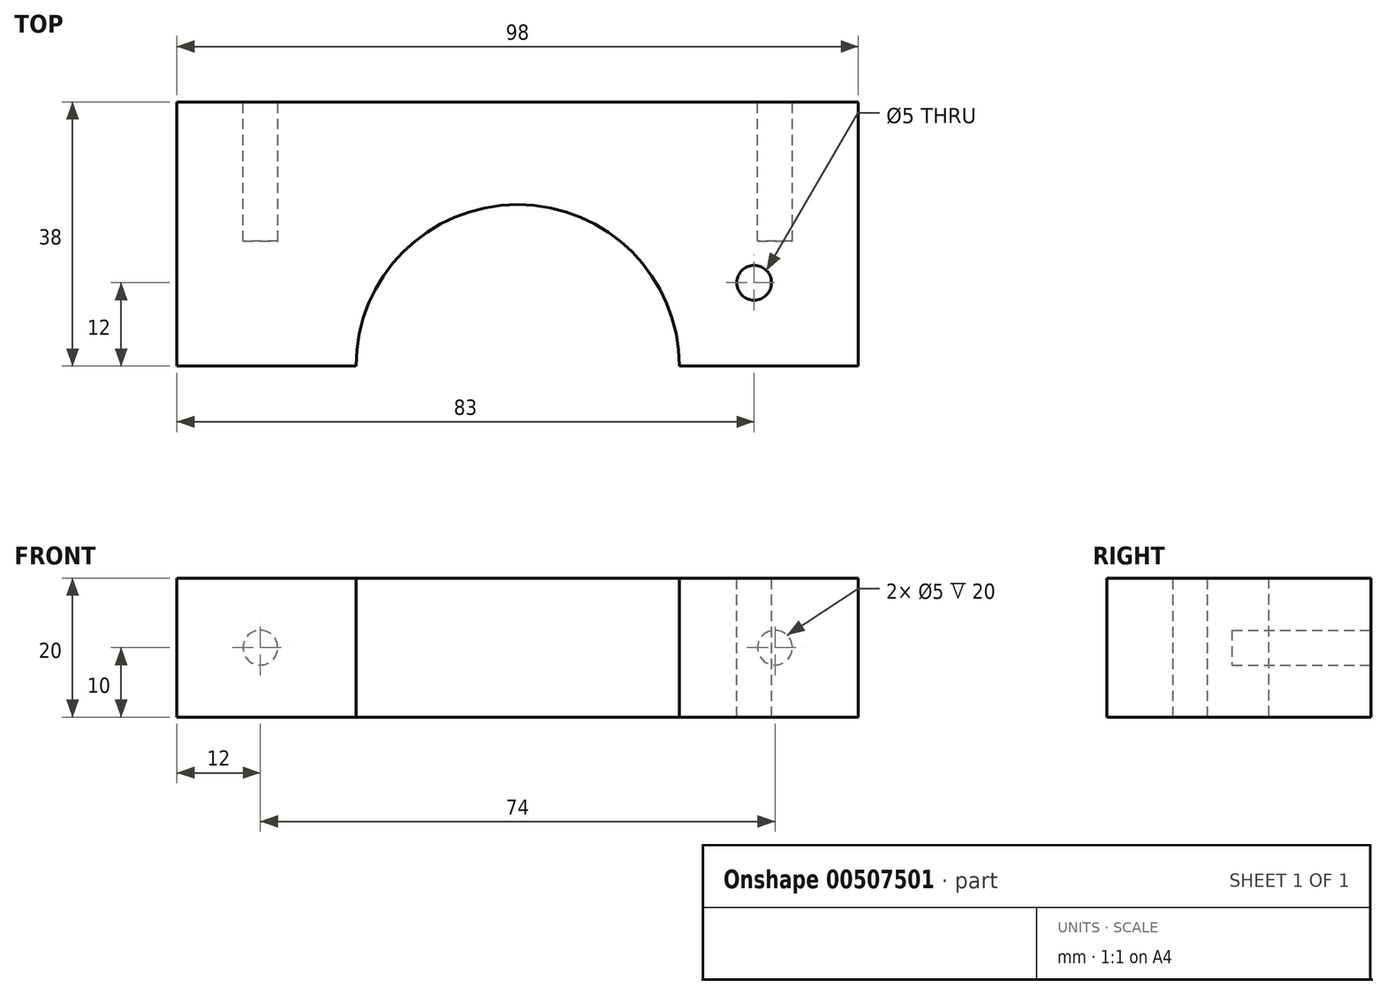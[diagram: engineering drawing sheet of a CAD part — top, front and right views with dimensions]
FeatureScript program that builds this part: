
annotation { "Feature Type Name" : "Feature", "Feature Type Description" : "" }
export const myFeature = defineFeature(function(context is Context, id is Id, definition is map)
    precondition{}
    {
        {
            var Q0;
            Q0=qCreatedBy(makeId("Top.planeOp"),FACE);
            var sketch = newSketch(context, id + "F0", { "sketchPlane" : qUnion([Q0])});
            skLineSegment(sketch, "E0.bottom", {"start": v(49, 19) * mm, "end": v(-49, 19) * mm});
            skLineSegment(sketch, "E0.left", {"start": v(49, 19) * mm, "end": v(49, -19) * mm});
            skLineSegment(sketch, "E0.right", {"start": v(-49, 19) * mm, "end": v(-49, -19) * mm});
            skPoint(sketch, "E0.middle", {"position": v(0, 0) * mm});
            skPoint(sketch, "E1.center.orphan", {"position": v(0, -19) * mm});
            skLineSegment(sketch, "E2", {"start": v(-49, -19) * mm, "end": v(-23.25, -19) * mm});
            skArc(sketch, "E3", {"start": v(23.25, -19) * mm, "mid": v(0, 4.25) * mm, "end": v(-23.25, -19) * mm});
            skLineSegment(sketch, "E4.trimOffspring", {"start": v(23.25, -19) * mm, "end": v(49, -19) * mm});
            skSolve(sketch);
        }
        {
            var Q0;
            Q0 = qSketchRegion(id + "F0", true);
            extrude(context, id + "F1", {"entities" : qUnion([Q0]), "depth" : 20 * mm});
        }
        {
            var Q0;
            Q0=makeQuery(id+"F1.opExtrude","SWEPT_FACE",FACE,{"disambiguationData":[OSD([sQuery(id+"F0.wireOp",EDGE,"E0.bottom")])]});
            var sketch = newSketch(context, id + "F2", { "sketchPlane" : qUnion([Q0])});
            skCircle(sketch, "E5", {"center": v(-37, 10) * mm, "radius": 2.5 * mm});
            skPoint(sketch, "E5.centerSnap0", {"position": v(-49, 10) * mm});
            skCircle(sketch, "E6", {"center": v(37, 10) * mm, "radius": 2.5 * mm});
            skSolve(sketch);
        }
        {
            var Q0;
            Q0=makeQuery(id+"F2.imprint","IMPRINT",FACE,{"disambiguationData":[TD([[makeQuery(id+"F2.imprint","IMPRINT",EDGE,{"derivedFrom":sQuery(id+"F2.wireOp",EDGE,"E5")}),1.0]])]});
            var Q1;
            Q1=makeQuery(id+"F2.imprint","IMPRINT",FACE,{"disambiguationData":[TD([[makeQuery(id+"F2.imprint","IMPRINT",EDGE,{"derivedFrom":sQuery(id+"F2.wireOp",EDGE,"E6")}),1.0]])]});
            extrude(context, id + "F3", {"entities" : qUnion([Q0, Q1]), "operationType" : NewBodyOperationType.REMOVE, "oppositeDirection" : true, "depth" : 20 * mm});
        }
        {
            var Q0;
            Q0=makeQuery(id+"F1.opExtrude","CAP_FACE",FACE,{"disambiguationData":[OSD([sQuery(id+"F0.wireOp",EDGE,"E0.bottom"),sQuery(id+"F0.wireOp",EDGE,"E0.left"),sQuery(id+"F0.wireOp",EDGE,"E0.right"),sQuery(id+"F0.wireOp",EDGE,"E2"),sQuery(id+"F0.wireOp",EDGE,"E3"),sQuery(id+"F0.wireOp",EDGE,"E4.trimOffspring")])],"isStart":false});
            var sketch = newSketch(context, id + "F4", { "sketchPlane" : qUnion([Q0])});
            skCircle(sketch, "E7", {"center": v(34, -7) * mm, "radius": 2.5 * mm});
            skSolve(sketch);
        }
        {
            var Q0;
            Q0=makeQuery(id+"F4.imprint","IMPRINT",FACE,{"disambiguationData":[TD([[makeQuery(id+"F4.imprint","IMPRINT",EDGE,{"derivedFrom":sQuery(id+"F4.wireOp",EDGE,"E7")}),1.0]])]});
            extrude(context, id + "F5", {"entities" : qUnion([Q0]), "operationType" : NewBodyOperationType.REMOVE, "oppositeDirection" : true, "depth" : 20 * mm});
        }
    });
